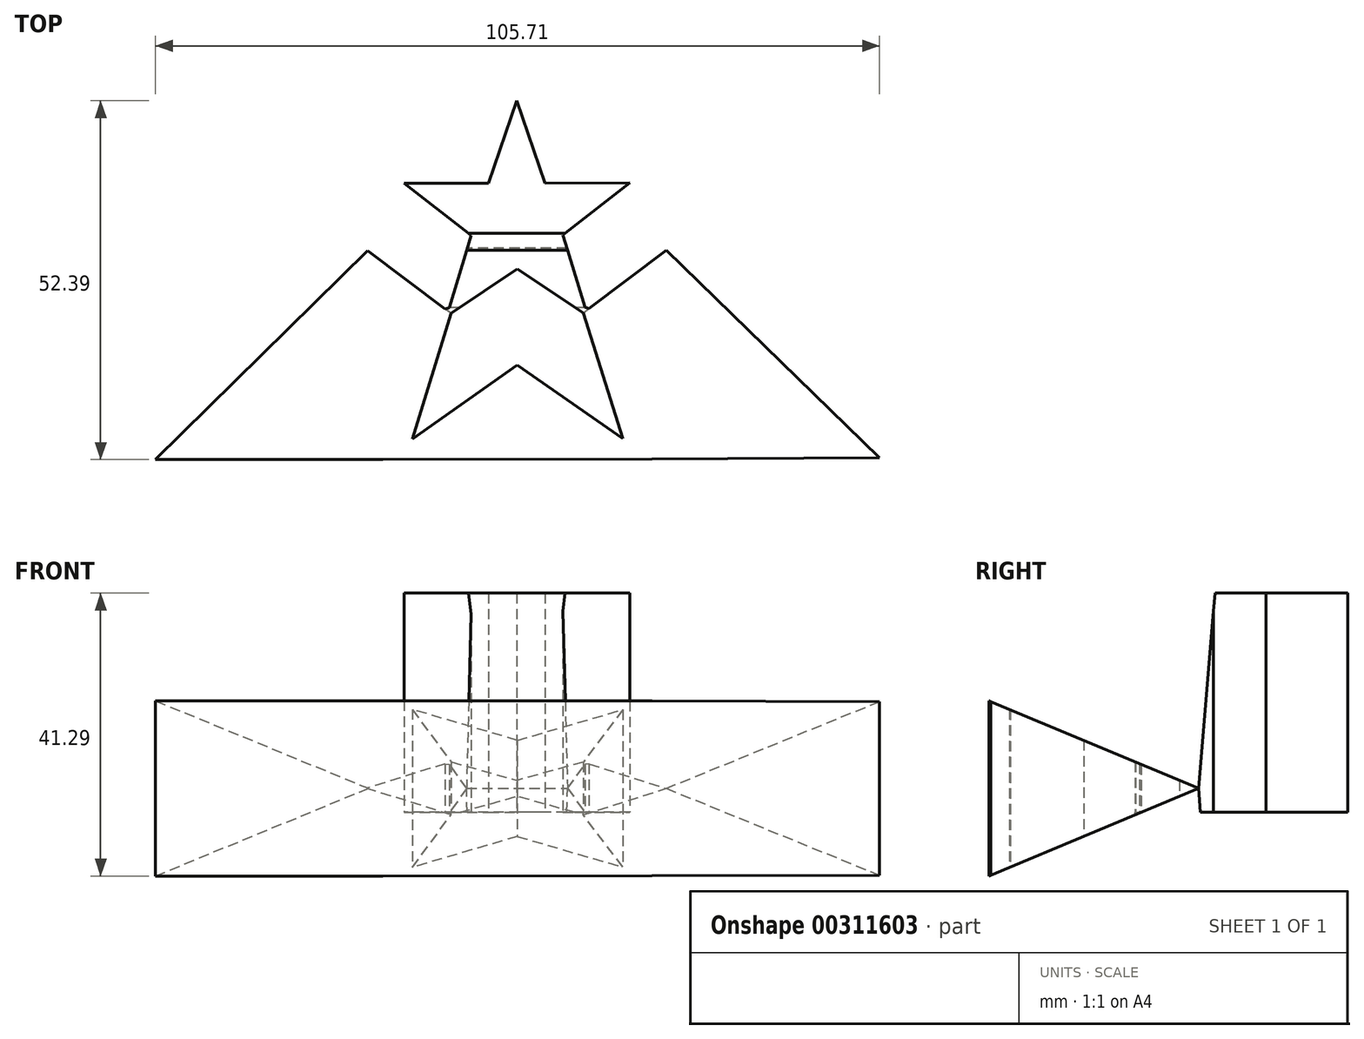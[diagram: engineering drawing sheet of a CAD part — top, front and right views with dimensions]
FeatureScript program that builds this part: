
annotation { "Feature Type Name" : "Feature", "Feature Type Description" : "" }
export const myFeature = defineFeature(function(context is Context, id is Id, definition is map)
    precondition{}
    {
        {
            var Q0;
            Q0=qCreatedBy(makeId("Top.planeOp"),FACE);
            var sketch = newSketch(context, id + "F0", { "sketchPlane" : qUnion([Q0])});
            skLineSegment(sketch, "E0", {"start": v(-22.23, 36.8) * mm, "end": v(-52.85, 6.7) * mm});
            skLineSegment(sketch, "E1", {"start": v(-52.85, 6.7) * mm, "end": v(-19.64, 6.7) * mm});
            skLineSegment(sketch, "E2", {"start": v(-0.03, 20.52) * mm, "end": v(-15.95, 9.3) * mm});
            skLineSegment(sketch, "E3", {"start": v(-6.8, 39.45) * mm, "end": v(-9.93, 28.89) * mm});
            skLineSegment(sketch, "E4", {"start": v(-9.7, 28.04) * mm, "end": v(-0.06, 34.52) * mm});
            skLineSegment(sketch, "E5", {"start": v(-6.8, 39.45) * mm, "end": v(-16.57, 47.05) * mm});
            skLineSegment(sketch, "E6", {"start": v(-16.57, 47.05) * mm, "end": v(-4.2, 47.05) * mm});
            skLineSegment(sketch, "E7", {"start": v(-4.2, 47.05) * mm, "end": v(-0.13, 59.1) * mm});
            skLineSegment(sketch, "E8", {"start": v(-15.38, 9.7) * mm, "end": v(-9.7, 28.04) * mm});
            skLineSegment(sketch, "E9", {"start": v(-9.7, 28.04) * mm, "end": v(-21.85, 37.18) * mm});
            skLineSegment(sketch, "E10", {"start": v(-22.23, 36.8) * mm, "end": v(-21.85, 37.18) * mm});
            skPoint(sketch, "E11.orphan", {"position": v(-22.23, 37.46) * mm});
            skLineSegment(sketch, "E12", {"start": v(-15.95, 9.3) * mm, "end": v(-19.64, 6.7) * mm});
            skPoint(sketch, "E13.orphan", {"position": v(0, 6.7) * mm});
            skLineSegment(sketch, "E14.MirrorCS", {"start": v(4.01, 47.07) * mm, "end": v(-0.13, 59.1) * mm});
            skLineSegment(sketch, "E15.MirrorCS", {"start": v(16.38, 47.13) * mm, "end": v(4.01, 47.07) * mm});
            skLineSegment(sketch, "E16.MirrorCS", {"start": v(6.64, 39.48) * mm, "end": v(16.38, 47.13) * mm});
            skLineSegment(sketch, "E17.MirrorCS", {"start": v(9.6, 28.09) * mm, "end": v(-0.06, 34.52) * mm});
            skLineSegment(sketch, "E18.MirrorCS", {"start": v(6.64, 39.48) * mm, "end": v(9.84, 28.92) * mm});
            skLineSegment(sketch, "E19.MirrorCS", {"start": v(9.6, 28.09) * mm, "end": v(21.71, 37.3) * mm});
            skLineSegment(sketch, "E20.MirrorCS", {"start": v(22.1, 36.92) * mm, "end": v(52.86, 6.97) * mm});
            skLineSegment(sketch, "E21.MirrorCS", {"start": v(22.1, 36.92) * mm, "end": v(21.71, 37.3) * mm});
            skLineSegment(sketch, "E22.MirrorCS", {"start": v(15.38, 9.78) * mm, "end": v(9.6, 28.09) * mm});
            skLineSegment(sketch, "E23.MirrorCS", {"start": v(-0.03, 20.52) * mm, "end": v(15.95, 9.38) * mm});
            skLineSegment(sketch, "E24.MirrorCS", {"start": v(15.95, 9.38) * mm, "end": v(19.66, 6.8) * mm});
            skLineSegment(sketch, "E25.MirrorCS", {"start": v(52.86, 6.97) * mm, "end": v(19.66, 6.8) * mm});
            skLineSegment(sketch, "E26", {"start": v(-19.64, 6.7) * mm, "end": v(19.66, 6.8) * mm});
            skPoint(sketch, "E27.orphan", {"position": v(0, 10.05) * mm});
            skLineSegment(sketch, "E28", {"start": v(-10.57, 28.69) * mm, "end": v(-9.93, 28.89) * mm});
            skPoint(sketch, "E29.orphan", {"position": v(0, 34.56) * mm});
            skPoint(sketch, "E30.orphan", {"position": v(0, 20.53) * mm});
            skLineSegment(sketch, "E31", {"start": v(0, 34.56) * mm, "end": v(0, 34.48) * mm});
            skLineSegment(sketch, "E32.MirrorCS", {"start": v(10.45, 28.73) * mm, "end": v(9.93, 28.89) * mm});
            skPoint(sketch, "E33.orphan", {"position": v(10.57, 28.69) * mm});
            skLineSegment(sketch, "E34", {"start": v(9.93, 28.89) * mm, "end": v(9.84, 28.92) * mm});
            skSolve(sketch);
        }
        {
            var Q0;
            Q0=makeQuery(id+"F0.imprint","IMPRINT",FACE,{"disambiguationData":[TD([[makeQuery(id+"F0.imprint","IMPRINT",EDGE,{"derivedFrom":sQuery(id+"F0.wireOp",EDGE,"E0")}),1.0]])]});
            var Q1;
            Q1=makeQuery(id+"F0.imprint","IMPRINT",FACE,{"disambiguationData":[TD([[makeQuery(id+"F0.imprint","IMPRINT",EDGE,{"derivedFrom":sQuery(id+"F0.wireOp",EDGE,"E20.MirrorCS")}),-1.0]])]});
            extrude(context, id + "F1", {"entities" : qUnion([Q0, Q1]), "depth" : 7 * mm});
        }
        {
            var Q0;
            {var subQ4=sQuery(id+"F0.wireOp",EDGE,"E12");Q0=makeQuery(id+"F0.imprint","IMPRINT",FACE,{"disambiguationData":[TD([[makeQuery(id+"F0.imprint","IMPRINT",EDGE,{"derivedFrom":subQ4}),1.0]])]});}
            var Q1;
            Q1=makeQuery(id+"F0.imprint","IMPRINT",FACE,{"disambiguationData":[TD([[makeQuery(id+"F0.imprint","IMPRINT",EDGE,{"derivedFrom":sQuery(id+"F0.wireOp",EDGE,"E3")}),1.0]])]});
            extrude(context, id + "F2", {"entities" : qUnion([Q0, Q1]), "depth" : 7 * mm});
        }
        {
            var Q0;
            Q0=makeQuery(id+"F1.opExtrude","CAP_FACE",FACE,{"disambiguationData":[OSD([sQuery(id+"F0.wireOp",EDGE,"E19.MirrorCS"),sQuery(id+"F0.wireOp",EDGE,"E20.MirrorCS"),sQuery(id+"F0.wireOp",EDGE,"E21.MirrorCS"),sQuery(id+"F0.wireOp",EDGE,"E22.MirrorCS"),sQuery(id+"F0.wireOp",EDGE,"E23.MirrorCS"),sQuery(id+"F0.wireOp",EDGE,"E24.MirrorCS"),sQuery(id+"F0.wireOp",EDGE,"E25.MirrorCS")])],"isStart":false});
            var Q1;
            Q1=makeQuery(id+"F1.opExtrude","CAP_FACE",FACE,{"disambiguationData":[OSD([sQuery(id+"F0.wireOp",EDGE,"E0"),sQuery(id+"F0.wireOp",EDGE,"E1"),sQuery(id+"F0.wireOp",EDGE,"E2"),sQuery(id+"F0.wireOp",EDGE,"E8"),sQuery(id+"F0.wireOp",EDGE,"E9"),sQuery(id+"F0.wireOp",EDGE,"E10"),sQuery(id+"F0.wireOp",EDGE,"E12")])],"isStart":false});
            extrude(context, id + "F3", {"entities" : qUnion([Q0, Q1]), "operationType" : NewBodyOperationType.ADD, "depth" : 25 * mm});
        }
        {
            var Q0;
            Q0=makeQuery(id+"F0.imprint","IMPRINT",FACE,{"disambiguationData":[TD([[makeQuery(id+"F0.imprint","IMPRINT",EDGE,{"derivedFrom":sQuery(id+"F0.wireOp",EDGE,"E20.MirrorCS")}),-1.0]])]});
            var Q1;
            Q1=makeQuery(id+"F0.imprint","IMPRINT",FACE,{"disambiguationData":[TD([[makeQuery(id+"F0.imprint","IMPRINT",EDGE,{"derivedFrom":sQuery(id+"F0.wireOp",EDGE,"E0")}),1.0]])]});
            extrude(context, id + "F4", {"entities" : qUnion([Q0, Q1]), "operationType" : NewBodyOperationType.ADD, "oppositeDirection" : true, "depth" : 25 * mm});
        }
        {
            var Q0;
            {var subQ4=sQuery(id+"F0.wireOp",EDGE,"E12");Q0=makeQuery(id+"F0.imprint","IMPRINT",FACE,{"disambiguationData":[TD([[makeQuery(id+"F0.imprint","IMPRINT",EDGE,{"derivedFrom":subQ4}),1.0]])]});}
            extrude(context, id + "F5", {"entities" : qUnion([Q0]), "operationType" : NewBodyOperationType.ADD, "oppositeDirection" : true, "depth" : 25 * mm});
        }
        {
            var Q0;
            Q0=makeQuery(id+"F2.opExtrude","CAP_FACE",FACE,{"disambiguationData":[OSD([sQuery(id+"F0.wireOp",EDGE,"E2"),sQuery(id+"F0.wireOp",EDGE,"E12"),sQuery(id+"F0.wireOp",EDGE,"E23.MirrorCS"),sQuery(id+"F0.wireOp",EDGE,"E24.MirrorCS"),sQuery(id+"F0.wireOp",EDGE,"E26")])],"isStart":false});
            extrude(context, id + "F6", {"entities" : qUnion([Q0]), "operationType" : NewBodyOperationType.ADD, "depth" : 25 * mm});
        }
        {
            var Q0;
            Q0=qCreatedBy(makeId("Right.planeOp"),FACE);
            var sketch = newSketch(context, id + "F7", { "sketchPlane" : qUnion([Q0])});
            skPoint(sketch, "E35.0", {"position": v(37.3, 3.5) * mm});
            skPoint(sketch, "E36.0", {"position": v(28.92, 7) * mm});
            skPoint(sketch, "E37.0", {"position": v(28.73, 7) * mm});
            skLineSegment(sketch, "E38", {"start": v(37.3, 3.5) * mm, "end": v(28.92, 7) * mm});
            skLineSegment(sketch, "E39", {"start": v(28.92, 7) * mm, "end": v(3.49, 17.63) * mm});
            skLineSegment(sketch, "E40", {"start": v(3.49, 17.63) * mm, "end": v(3.49, 37.9) * mm});
            skLineSegment(sketch, "E41", {"start": v(3.49, 37.9) * mm, "end": v(40.2, 37.9) * mm});
            skLineSegment(sketch, "E42", {"start": v(40.2, 37.9) * mm, "end": v(37.3, 3.5) * mm});
            skLineSegment(sketch, "E43", {"start": v(37.3, 3.5) * mm, "end": v(0, 3.5) * mm, "construction": true});
            skLineSegment(sketch, "E44.MirrorCS", {"start": v(28.92, 0) * mm, "end": v(3.49, -10.63) * mm});
            skLineSegment(sketch, "E45.MirrorCS", {"start": v(40.2, -30.9) * mm, "end": v(37.3, 3.5) * mm});
            skLineSegment(sketch, "E46.MirrorCS", {"start": v(37.3, 3.5) * mm, "end": v(28.92, 0) * mm});
            skLineSegment(sketch, "E47.MirrorCS", {"start": v(3.49, -30.9) * mm, "end": v(40.2, -30.9) * mm});
            skLineSegment(sketch, "E48.MirrorCS", {"start": v(3.49, -10.63) * mm, "end": v(3.49, -30.9) * mm});
            skSolve(sketch);
        }
        {
            var Q0;
            Q0=makeQuery(id+"F7.imprint","IMPRINT",FACE,{"disambiguationData":[TD([[makeQuery(id+"F7.imprint","IMPRINT",EDGE,{"derivedFrom":sQuery(id+"F7.wireOp",EDGE,"E38")}),-1.0]])]});
            var Q1;
            Q1=makeQuery(id+"F7.imprint","IMPRINT",FACE,{"disambiguationData":[TD([[makeQuery(id+"F7.imprint","IMPRINT",EDGE,{"derivedFrom":sQuery(id+"F7.wireOp",EDGE,"E44.MirrorCS")}),1.0]])]});
            extrude(context, id + "F8", {"entities" : qUnion([Q0, Q1]), "operationType" : NewBodyOperationType.REMOVE, "endBound" : BoundingType.THROUGH_ALL, "oppositeDirection" : true, "depth" : 25 * mm, "hasSecondDirection" : true, "secondDirectionBound" : SecondDirectionBoundingType.THROUGH_ALL, "secondDirectionOppositeDirection" : false, "secondDirectionDepth" : 25 * mm});
        }
    });
